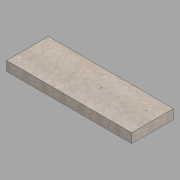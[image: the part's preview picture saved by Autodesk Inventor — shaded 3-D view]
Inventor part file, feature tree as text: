
AUTODESK INVENTOR PART (.ipt)
format: ipt  version: 2022 (Build 260153000, 153)  size: 133,632 bytes
history: native  units: in
note: dims shown in document units (in); Inventor stores cm internally (conversion verified against a paired STEP export)
features: extrude x2, sketch x2, other x1
ambient origin geometry x8: Origin, YZ Plane, XZ Plane, XY Plane, X Axis, Y Axis, Z Axis, Center Point
bodies: Body1 (feature_tree)
feature tree (5):
  other  "Bridge cap"
  extrude  "Extrusion1"  Depth=16.0in
  extrude  "Extrusion2"  Depth=3.625in
  sketch  "Sketch1"  dims[d0=48.0in d1=16.0in]
  sketch  "Sketch2"  dims[d2=3.625in d3=0.0in d4=0.25in d5=0.25in d6=0.1875in d7=2.7559in d9=0.5in d10=0.3937in d12=12.0in d14=0.1875in d15=0.0in d16=0.0in]
